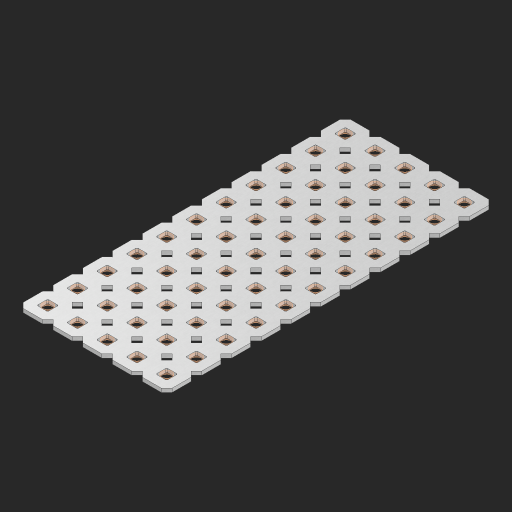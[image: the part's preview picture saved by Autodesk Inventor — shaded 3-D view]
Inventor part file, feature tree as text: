
AUTODESK INVENTOR PART (.ipt)
format: ipt  version: 2023 (Build 270158000, 158)  size: 934,912 bytes
history: native  units: in
note: dims shown in document units (in); Inventor stores cm internally (conversion verified against a paired STEP export)
features: other x56, extrude x54, sketch x2, pattern_linear x1
ambient origin geometry x8: Origin, YZ Plane, XZ Plane, XY Plane, X Axis, Y Axis, Z Axis, Center Point
bodies: Solid1 (feature_tree), Body (feature_tree)
feature tree (113):
  pattern_linear  "Rectangular Pattern1"  Spacing1=0.09in  [1 undecoded]
  sketch  "Sketch1"  dims[d1=0.5in]
  sketch  "Sketch2"  dims[d2=0.182in d3=0.09in d4=0.09in d5=0.09in d6=0.09in d7=0.09in d8=0.09in d9=0.09in d10=0.09in d11=0.02in d13=0.0in d14=0.172in d15=0.0625in d16=0.0in d19=0.5in d22=0.5in]
  other  "Srf1"
  other  "Srf126"
  other  "Srf127"
  other  "Srf128"
  other  "Srf129"
  other  "Srf130"
  other  "Srf131"
  other  "Srf250"
  other  "Srf251"
  other  "Srf252"
  other  "Srf253"
  other  "Srf268"
  other  "Srf269"
  other  "Srf270"
  other  "Srf271"
  other  "Srf272"
  other  "Srf273"
  other  "Srf274"
  other  "Srf275"
  other  "Srf276"
  other  "Srf277"
  other  "Srf278"
  other  "Srf293"
  other  "Srf294"
  other  "Srf295"
  other  "Srf296"
  other  "Srf297"
  other  "Srf298"
  other  "Srf299"
  other  "Srf300"
  other  "Srf301"
  other  "Srf302"
  other  "Srf303"
  other  "Srf318"
  other  "Srf319"
  other  "Srf320"
  other  "Srf321"
  other  "Srf322"
  other  "Srf323"
  other  "Srf324"
  other  "Srf325"
  other  "Srf326"
  other  "Srf327"
  other  "Srf328"
  other  "Srf343"
  other  "Srf344"
  other  "Srf345"
  other  "Srf346"
  other  "Srf347"
  other  "Srf348"
  other  "Srf349"
  other  "Srf350"
  other  "Srf351"
  other  "Srf352"
  other  "Srf353"
  other  "Circle"
  extrude  "ExtrusionSrf126"  Depth=0.09in
  extrude  "ExtrusionSrf127"  Depth=0.09in
  extrude  "ExtrusionSrf128"  Depth=0.09in
  extrude  "ExtrusionSrf129"  Depth=0.09in
  extrude  "ExtrusionSrf130"  Depth=0.09in
  extrude  "ExtrusionSrf131"  Depth=0.09in
  extrude  "ExtrusionSrf250"  Depth=0.09in
  extrude  "ExtrusionSrf251"  Depth=0.02in
  extrude  "ExtrusionSrf252"  TaperAngle=0.0deg  [1 undecoded]
  extrude  "ExtrusionSrf253"  Depth=0.5in
  extrude  "ExtrusionSrf268"  Depth=0.0625in TaperAngle=0.0deg
  extrude  "ExtrusionSrf269"  Depth=0.5in
  extrude  "ExtrusionSrf270"  Depth=0.5in
  extrude  "ExtrusionSrf271"  [1 undecoded]
  extrude  "ExtrusionSrf272"  [1 undecoded]
  extrude  "ExtrusionSrf273"  [1 undecoded]
  extrude  "ExtrusionSrf274"  [1 undecoded]
  extrude  "ExtrusionSrf275"  [1 undecoded]
  extrude  "ExtrusionSrf276"  [1 undecoded]
  extrude  "ExtrusionSrf277"  [1 undecoded]
  extrude  "ExtrusionSrf278"  [1 undecoded]
  extrude  "ExtrusionSrf293"  [1 undecoded]
  extrude  "ExtrusionSrf294"  [1 undecoded]
  extrude  "ExtrusionSrf295"  [1 undecoded]
  extrude  "ExtrusionSrf296"  [1 undecoded]
  extrude  "ExtrusionSrf297"  [1 undecoded]
  extrude  "ExtrusionSrf298"  [1 undecoded]
  extrude  "ExtrusionSrf299"  [1 undecoded]
  extrude  "ExtrusionSrf300"  [1 undecoded]
  extrude  "ExtrusionSrf301"  [1 undecoded]
  extrude  "ExtrusionSrf302"  [1 undecoded]
  extrude  "ExtrusionSrf303"  [1 undecoded]
  extrude  "ExtrusionSrf318"  [1 undecoded]
  extrude  "ExtrusionSrf319"  [1 undecoded]
  extrude  "ExtrusionSrf320"  [1 undecoded]
  extrude  "ExtrusionSrf321"  [1 undecoded]
  extrude  "ExtrusionSrf322"  [1 undecoded]
  extrude  "ExtrusionSrf323"  [1 undecoded]
  extrude  "ExtrusionSrf324"  [1 undecoded]
  extrude  "ExtrusionSrf325"  [1 undecoded]
  extrude  "ExtrusionSrf326"  [1 undecoded]
  extrude  "ExtrusionSrf327"  [1 undecoded]
  extrude  "ExtrusionSrf328"  [1 undecoded]
  extrude  "ExtrusionSrf343"  [1 undecoded]
  extrude  "ExtrusionSrf344"  [1 undecoded]
  extrude  "ExtrusionSrf345"  [1 undecoded]
  extrude  "ExtrusionSrf346"  [1 undecoded]
  extrude  "ExtrusionSrf347"  [1 undecoded]
  extrude  "ExtrusionSrf348"  [1 undecoded]
  extrude  "ExtrusionSrf349"  [1 undecoded]
  extrude  "ExtrusionSrf350"  [1 undecoded]
  extrude  "ExtrusionSrf351"  [1 undecoded]
  extrude  "ExtrusionSrf352"  [1 undecoded]
  extrude  "ExtrusionSrf353"  [1 undecoded]
note: 43 required parameter values undecoded (feature->parameter linkage not recoverable at this tier; creation-order binding heuristic only, values carry confidence <= 0.55)
